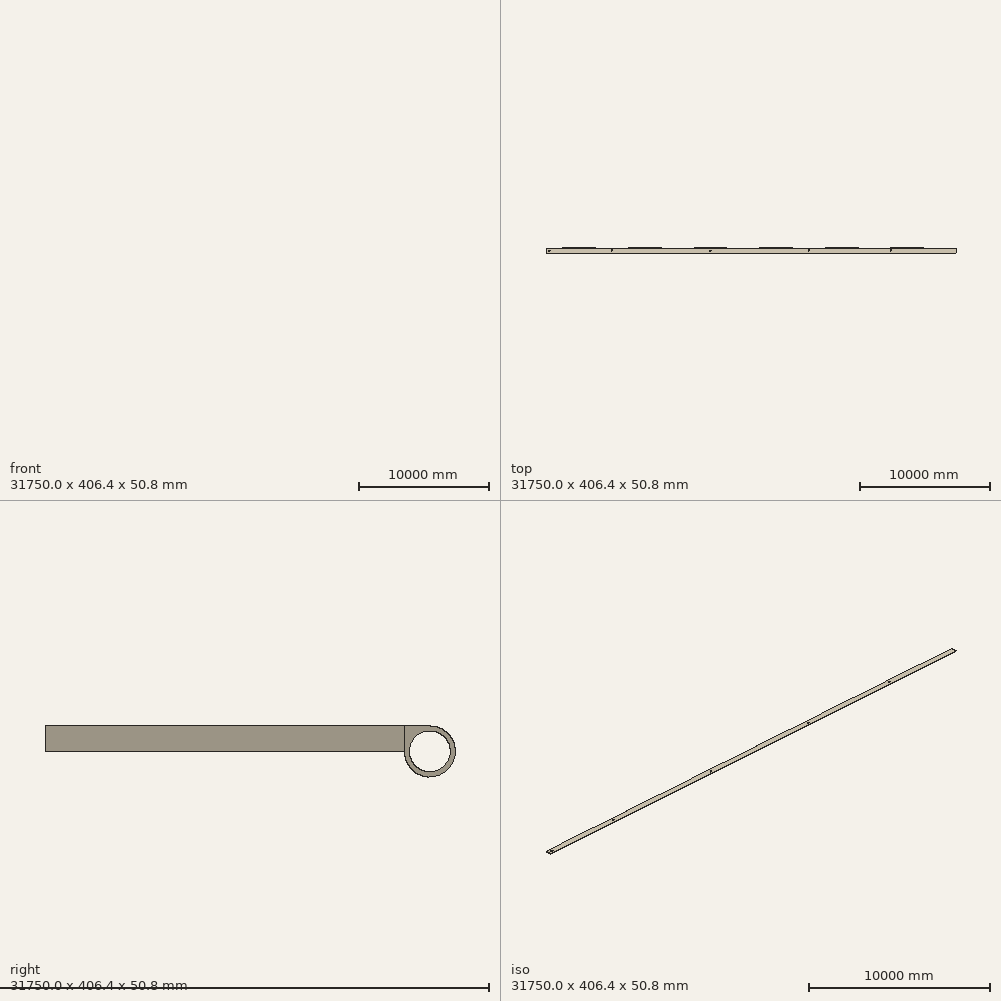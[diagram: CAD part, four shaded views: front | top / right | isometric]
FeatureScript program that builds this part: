
annotation { "Feature Type Name" : "Feature", "Feature Type Description" : "" }
export const myFeature = defineFeature(function(context is Context, id is Id, definition is map)
    precondition{}
    {
        {
            var Q0;
            Q0=qCreatedBy(makeId("Top.planeOp"),FACE);
            var sketch = newSketch(context, id + "F0", { "sketchPlane" : qUnion([Q0])});
            skLineSegment(sketch, "E0.bottom", {"start": v(-32840.86, 344.6) * mm, "end": v(-1090.86, 344.6) * mm});
            skLineSegment(sketch, "E0.top", {"start": v(-32840.86, -36.4) * mm, "end": v(-1090.86, -36.4) * mm});
            skLineSegment(sketch, "E0.left", {"start": v(-32840.86, 344.6) * mm, "end": v(-32840.86, -36.4) * mm});
            skLineSegment(sketch, "E0.right", {"start": v(-1090.86, 344.6) * mm, "end": v(-1090.86, -36.4) * mm});
            skSolve(sketch);
        }
        {
            var Q0;
            Q0 = qSketchRegion(id + "F0", true);
            extrude(context, id + "F1", {"entities" : qUnion([Q0]), "depth" : 25.4 * mm, "offsetDistance" : 25.4 * mm});
        }
        {
            var Q0;
            Q0=makeQuery(id+"F1.opExtrude","SWEPT_FACE",FACE,{"disambiguationData":[OSD([sQuery(id+"F0.wireOp",EDGE,"E0.right")])]});
            var sketch = newSketch(context, id + "F2", { "sketchPlane" : qUnion([Q0])});
            skCircle(sketch, "E1", {"center": v(344.6, 0) * mm, "radius": 25.4 * mm});
            skSolve(sketch);
        }
        {
            var Q0;
            {var subQ1=sQuery(id+"F0.wireOp",EDGE,"E0.right");var subQ2=makeQuery(id+"F1.opExtrude","SWEPT_EDGE",EDGE,{"disambiguationData":[OSD([sQuery(id+"F0.wireOp",EDGE,"E0.bottom"),subQ1])]});Q0=makeQuery(id+"F2.imprint","IMPRINT",FACE,{"disambiguationData":[TD([[makeQuery(id+"F2.imprint","IMPRINT",EDGE,{"derivedFrom":subQ2}),1.0]])]});}
            var Q1;
            Q1=makeQuery(id+"F1.opExtrude","CAP_EDGE",EDGE,{"disambiguationData":[OSD([sQuery(id+"F0.wireOp",EDGE,"E0.bottom")])],"isStart":false});
            sweep(context, id + "F3", {"operationType" : NewBodyOperationType.ADD, "profiles" : qUnion([Q0]), "path" : qUnion([Q1])});
        }
        {
            var Q0;
            {var subQ0=sQuery(id+"F0.wireOp",EDGE,"E0.right");Q0=makeQuery(id+"F3.boolean.opBoolean","MERGE",FACE,{"derivedFrom":[makeQuery(id+"F1.opExtrude","SWEPT_FACE",FACE,{"disambiguationData":[OSD([subQ0])]}),makeQuery(id+"F3.opSweep","CAP_FACE",FACE,{"disambiguationData":[OSD([sQuery(id+"F0.wireOp",EDGE,"E0.bottom"),subQ0,sQuery(id+"F2.wireOp",EDGE,"E1")])],"isStart":true})]});}
            var sketch = newSketch(context, id + "F4", { "sketchPlane" : qUnion([Q0])});
            skCircle(sketch, "E2", {"center": v(344.6, 0) * mm, "radius": 20.32 * mm});
            skSolve(sketch);
        }
        {
            var Q0;
            Q0 = qSketchRegion(id + "F4", true);
            extrude(context, id + "F5", {"entities" : qUnion([Q0]), "operationType" : NewBodyOperationType.REMOVE, "endBound" : BoundingType.THROUGH_ALL, "oppositeDirection" : true, "depth" : 25.4 * mm, "offsetDistance" : 25.4 * mm});
        }
        {
            var Q0;
            Q0=makeQuery(id+"F1.opExtrude","CAP_FACE",FACE,{"disambiguationData":[OSD([sQuery(id+"F0.wireOp",EDGE,"E0.bottom"),sQuery(id+"F0.wireOp",EDGE,"E0.top"),sQuery(id+"F0.wireOp",EDGE,"E0.left"),sQuery(id+"F0.wireOp",EDGE,"E0.right")])],"isStart":true});
            var sketch = newSketch(context, id + "F6", { "sketchPlane" : qUnion([Q0])});
            skLineSegment(sketch, "E3.bottom", {"start": v(-1090.86, -319.2) * mm, "end": v(-3630.86, -319.2) * mm});
            skLineSegment(sketch, "E3.top", {"start": v(-1090.86, -497) * mm, "end": v(-3630.86, -497) * mm});
            skLineSegment(sketch, "E3.left", {"start": v(-1090.86, -319.2) * mm, "end": v(-1090.86, -497) * mm});
            skLineSegment(sketch, "E3.right", {"start": v(-3630.86, -319.2) * mm, "end": v(-3630.86, -497) * mm});
            skLineSegment(sketch, "E4.1.0.0", {"start": v(-3630.86, -497) * mm, "end": v(-6170.86, -497) * mm});
            skLineSegment(sketch, "E4.1.0.1", {"start": v(-3630.86, -319.2) * mm, "end": v(-6170.86, -319.2) * mm});
            skLineSegment(sketch, "E4.1.0.2", {"start": v(-6170.86, -319.2) * mm, "end": v(-6170.86, -497) * mm});
            skLineSegment(sketch, "E4.2.0.0", {"start": v(-6170.86, -497) * mm, "end": v(-8710.86, -497) * mm});
            skLineSegment(sketch, "E4.2.0.1", {"start": v(-6170.86, -319.2) * mm, "end": v(-8710.86, -319.2) * mm});
            skLineSegment(sketch, "E4.2.0.2", {"start": v(-8710.86, -319.2) * mm, "end": v(-8710.86, -497) * mm});
            skLineSegment(sketch, "E4.2.0.3", {"start": v(-6170.86, -319.2) * mm, "end": v(-6170.86, -497) * mm});
            skLineSegment(sketch, "E4.direction1", {"start": v(-3630.86, -497) * mm, "end": v(-6170.86, -497) * mm, "construction": true});
            skLineSegment(sketch, "E5.0.3.0", {"start": v(-8710.86, -497) * mm, "end": v(-11250.86, -497) * mm});
            skLineSegment(sketch, "E5.3.3.0", {"start": v(-8710.86, -319.2) * mm, "end": v(-11250.86, -319.2) * mm});
            skLineSegment(sketch, "E5.6.3.0", {"start": v(-11250.86, -319.2) * mm, "end": v(-11250.86, -497) * mm});
            skLineSegment(sketch, "E5.0.4.0", {"start": v(-11250.86, -497) * mm, "end": v(-13790.86, -497) * mm});
            skLineSegment(sketch, "E5.3.4.0", {"start": v(-11250.86, -319.2) * mm, "end": v(-13790.86, -319.2) * mm});
            skLineSegment(sketch, "E5.6.4.0", {"start": v(-13790.86, -319.2) * mm, "end": v(-13790.86, -497) * mm});
            skLineSegment(sketch, "E5.9.4.0", {"start": v(-11250.86, -319.2) * mm, "end": v(-11250.86, -497) * mm});
            skLineSegment(sketch, "E5.0.5.0", {"start": v(-13790.86, -497) * mm, "end": v(-16330.86, -497) * mm});
            skLineSegment(sketch, "E5.3.5.0", {"start": v(-13790.86, -319.2) * mm, "end": v(-16330.86, -319.2) * mm});
            skLineSegment(sketch, "E5.6.5.0", {"start": v(-16330.86, -319.2) * mm, "end": v(-16330.86, -497) * mm});
            skLineSegment(sketch, "E5.9.5.0", {"start": v(-13790.86, -319.2) * mm, "end": v(-13790.86, -497) * mm});
            skLineSegment(sketch, "E5.0.6.0", {"start": v(-16330.86, -497) * mm, "end": v(-18870.86, -497) * mm});
            skLineSegment(sketch, "E5.3.6.0", {"start": v(-16330.86, -319.2) * mm, "end": v(-18870.86, -319.2) * mm});
            skLineSegment(sketch, "E5.6.6.0", {"start": v(-18870.86, -319.2) * mm, "end": v(-18870.86, -497) * mm});
            skLineSegment(sketch, "E5.9.6.0", {"start": v(-16330.86, -319.2) * mm, "end": v(-16330.86, -497) * mm});
            skLineSegment(sketch, "E5.0.7.0", {"start": v(-18870.86, -497) * mm, "end": v(-21410.86, -497) * mm});
            skLineSegment(sketch, "E5.3.7.0", {"start": v(-18870.86, -319.2) * mm, "end": v(-21410.86, -319.2) * mm});
            skLineSegment(sketch, "E5.6.7.0", {"start": v(-21410.86, -319.2) * mm, "end": v(-21410.86, -497) * mm});
            skLineSegment(sketch, "E5.9.7.0", {"start": v(-18870.86, -319.2) * mm, "end": v(-18870.86, -497) * mm});
            skLineSegment(sketch, "E5.0.8.0", {"start": v(-21410.86, -497) * mm, "end": v(-23950.86, -497) * mm});
            skLineSegment(sketch, "E5.3.8.0", {"start": v(-21410.86, -319.2) * mm, "end": v(-23950.86, -319.2) * mm});
            skLineSegment(sketch, "E5.6.8.0", {"start": v(-23950.86, -319.2) * mm, "end": v(-23950.86, -497) * mm});
            skLineSegment(sketch, "E5.9.8.0", {"start": v(-21410.86, -319.2) * mm, "end": v(-21410.86, -497) * mm});
            skLineSegment(sketch, "E5.0.9.0", {"start": v(-23950.86, -497) * mm, "end": v(-26490.86, -497) * mm});
            skLineSegment(sketch, "E5.3.9.0", {"start": v(-23950.86, -319.2) * mm, "end": v(-26490.86, -319.2) * mm});
            skLineSegment(sketch, "E5.6.9.0", {"start": v(-26490.86, -319.2) * mm, "end": v(-26490.86, -497) * mm});
            skLineSegment(sketch, "E5.9.9.0", {"start": v(-23950.86, -319.2) * mm, "end": v(-23950.86, -497) * mm});
            skLineSegment(sketch, "E5.0.10.0", {"start": v(-26490.86, -497) * mm, "end": v(-29030.86, -497) * mm});
            skLineSegment(sketch, "E5.3.10.0", {"start": v(-26490.86, -319.2) * mm, "end": v(-29030.86, -319.2) * mm});
            skLineSegment(sketch, "E5.6.10.0", {"start": v(-29030.86, -319.2) * mm, "end": v(-29030.86, -497) * mm});
            skLineSegment(sketch, "E5.9.10.0", {"start": v(-26490.86, -319.2) * mm, "end": v(-26490.86, -497) * mm});
            skLineSegment(sketch, "E6.0.11.0", {"start": v(-29030.86, -497) * mm, "end": v(-31570.86, -497) * mm});
            skLineSegment(sketch, "E6.3.11.0", {"start": v(-29030.86, -319.2) * mm, "end": v(-31570.86, -319.2) * mm});
            skLineSegment(sketch, "E6.6.11.0", {"start": v(-31570.86, -319.2) * mm, "end": v(-31570.86, -497) * mm});
            skLineSegment(sketch, "E7.0.12.0", {"start": v(-31570.86, -497) * mm, "end": v(-34110.86, -497) * mm});
            skLineSegment(sketch, "E7.3.12.0", {"start": v(-31570.86, -319.2) * mm, "end": v(-34110.86, -319.2) * mm});
            skLineSegment(sketch, "E7.6.12.0", {"start": v(-34110.86, -319.2) * mm, "end": v(-34110.86, -497) * mm});
            skSolve(sketch);
        }
        {
            var Q0;
            Q0=makeQuery(id+"F6.imprint","IMPRINT",FACE,{"disambiguationData":[TD([[makeQuery(id+"F6.imprint","IMPRINT",EDGE,{"derivedFrom":sQuery(id+"F6.wireOp",EDGE,"E3.bottom")}),1.0]])]});
            var Q1;
            Q1=makeQuery(id+"F6.imprint","IMPRINT",FACE,{"disambiguationData":[TD([[makeQuery(id+"F6.imprint","IMPRINT",EDGE,{"derivedFrom":sQuery(id+"F6.wireOp",EDGE,"E4.2.0.0")}),-1.0]])]});
            var Q2;
            Q2=makeQuery(id+"F6.imprint","IMPRINT",FACE,{"disambiguationData":[TD([[makeQuery(id+"F6.imprint","IMPRINT",EDGE,{"derivedFrom":sQuery(id+"F6.wireOp",EDGE,"E5.0.4.0")}),-1.0]])]});
            var Q3;
            Q3=makeQuery(id+"F6.imprint","IMPRINT",FACE,{"disambiguationData":[TD([[makeQuery(id+"F6.imprint","IMPRINT",EDGE,{"derivedFrom":sQuery(id+"F6.wireOp",EDGE,"E5.0.6.0")}),-1.0]])]});
            var Q4;
            Q4=makeQuery(id+"F6.imprint","IMPRINT",FACE,{"disambiguationData":[TD([[makeQuery(id+"F6.imprint","IMPRINT",EDGE,{"derivedFrom":sQuery(id+"F6.wireOp",EDGE,"E5.0.8.0")}),-1.0]])]});
            var Q5;
            Q5=makeQuery(id+"F6.imprint","IMPRINT",FACE,{"disambiguationData":[TD([[makeQuery(id+"F6.imprint","IMPRINT",EDGE,{"derivedFrom":sQuery(id+"F6.wireOp",EDGE,"E5.0.10.0")}),-1.0]])]});
            var Q6;
            Q6=makeQuery(id+"F6.imprint","IMPRINT",FACE,{"disambiguationData":[TD([[makeQuery(id+"F6.imprint","IMPRINT",EDGE,{"derivedFrom":sQuery(id+"F6.wireOp",EDGE,"E7.0.12.0")}),-1.0]])]});
            extrude(context, id + "F7", {"entities" : qUnion([Q0, Q1, Q2, Q3, Q4, Q5, Q6]), "operationType" : NewBodyOperationType.REMOVE, "endBound" : BoundingType.SYMMETRIC, "oppositeDirection" : true, "depth" : 254 * mm, "offsetDistance" : 25.4 * mm});
        }
        {
            var Q0;
            Q0=makeQuery(id+"F1.opExtrude","CAP_FACE",FACE,{"disambiguationData":[OSD([sQuery(id+"F0.wireOp",EDGE,"E0.bottom"),sQuery(id+"F0.wireOp",EDGE,"E0.top"),sQuery(id+"F0.wireOp",EDGE,"E0.left"),sQuery(id+"F0.wireOp",EDGE,"E0.right")])],"isStart":true});
            var sketch = newSketch(context, id + "F8", { "sketchPlane" : qUnion([Q0])});
            skLineSegment(sketch, "E8", {"start": v(-32840.86, -141.4) * mm, "end": v(179.14, -141.4) * mm, "construction": true});
            skPoint(sketch, "E8.startSnap0", {"position": v(-32840.86, -141.4) * mm});
            skPoint(sketch, "E9", {"position": v(-27760.86, -141.4) * mm});
            skPoint(sketch, "E10", {"position": v(-20140.86, -141.4) * mm});
            skPoint(sketch, "E11", {"position": v(-12520.86, -141.4) * mm});
            skPoint(sketch, "E12", {"position": v(-6170.86, -141.4) * mm});
            skPoint(sketch, "E13", {"position": v(-32586.86, -141.4) * mm});
            skPoint(sketch, "E14", {"position": v(-74.86, -141.4) * mm});
            skSolve(sketch);
        }
        {
            var Q0;
            Q0=sQuery(id+"F8.wireOp",VERTEX,"E13");
            var Q1;
            Q1=sQuery(id+"F8.wireOp",VERTEX,"E9");
            var Q2;
            Q2=sQuery(id+"F8.wireOp",VERTEX,"E10");
            var Q3;
            Q3=sQuery(id+"F8.wireOp",VERTEX,"E11");
            var Q4;
            Q4=sQuery(id+"F8.wireOp",VERTEX,"E12");
            var Q5;
            Q5=sQuery(id+"F8.wireOp",VERTEX,"E14");
            var Q6;
            Q6=makeQuery(id+"F1.opExtrude","SWEPT_BODY",BODY,{"disambiguationData":[OSD([sQuery(id+"F0.wireOp",EDGE,"E0.bottom"),sQuery(id+"F0.wireOp",EDGE,"E0.top"),sQuery(id+"F0.wireOp",EDGE,"E0.left"),sQuery(id+"F0.wireOp",EDGE,"E0.right")])]});
            hole(context, id + "F9", {"style" : HoleStyle.C_SINK, "endStyle" : HoleEndStyle.THROUGH, "holeDiameter" : 101.6 * mm, "cSinkDiameter" : 203.2 * mm, "cSinkAngle" : 110 * degree, "majorDiameter" : 6.35 * mm, "isTappedThrough" : true, "tappedDepth" : 12.7 * mm, "tapClearance" : 3, "locations" : qUnion([Q0, Q1, Q2, Q3, Q4, Q5]), "scope" : qUnion([Q6])});
        }
    });
